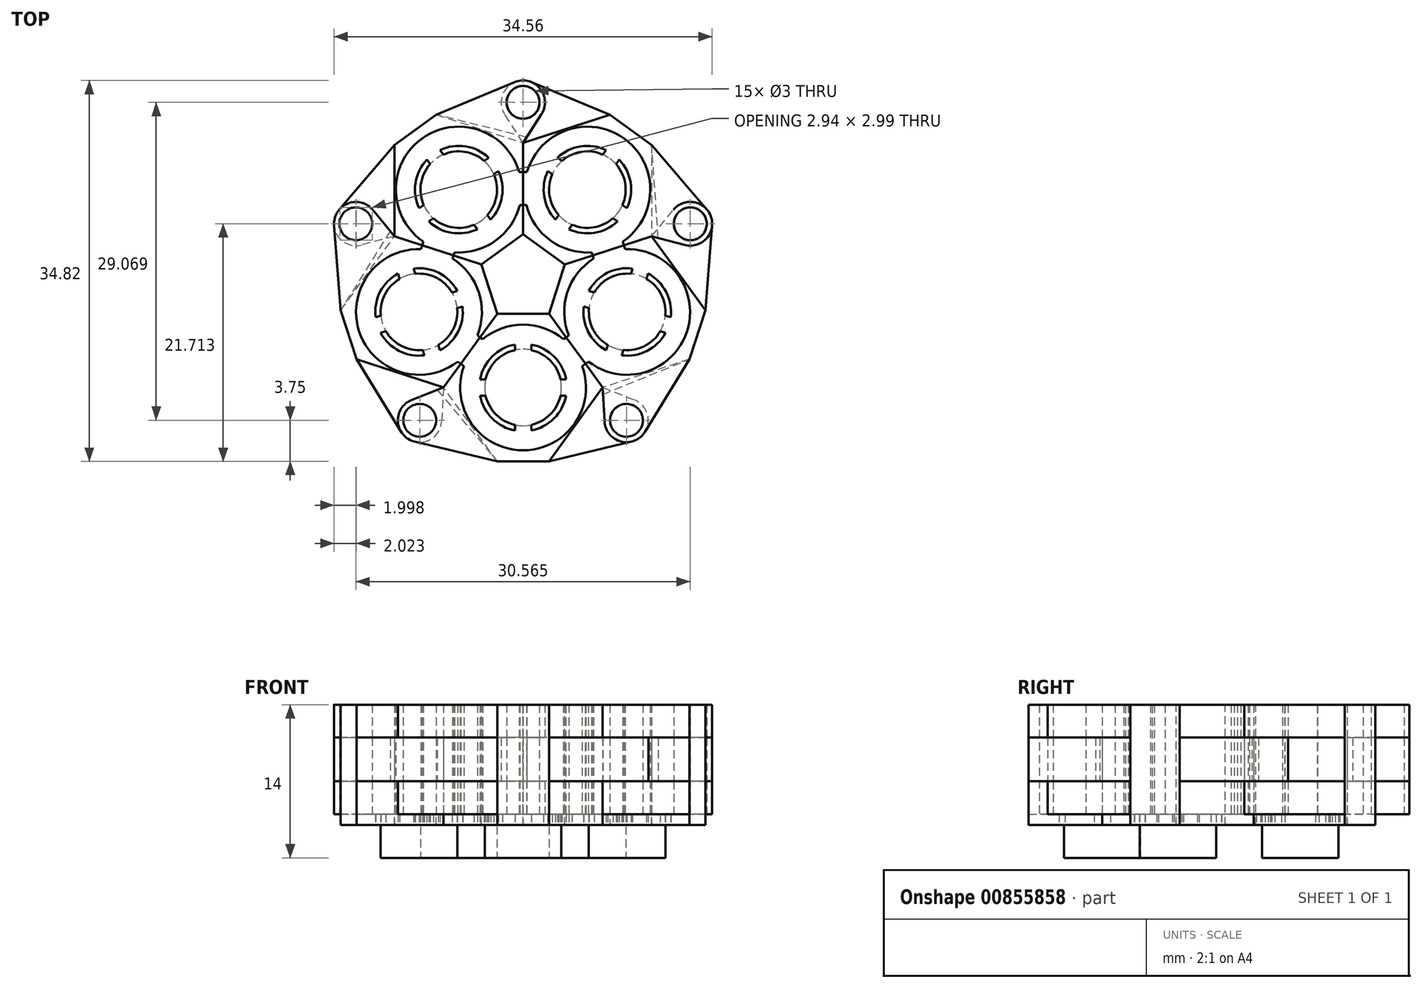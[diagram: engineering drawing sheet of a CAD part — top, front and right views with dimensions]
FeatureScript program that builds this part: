
annotation { "Feature Type Name" : "Feature", "Feature Type Description" : "" }
export const myFeature = defineFeature(function(context is Context, id is Id, definition is map)
    precondition{}
    {
        {
            var Q0;
            Q0=qCreatedBy(makeId("Top.planeOp"),FACE);
            var sketch = newSketch(context, id + "F0", { "sketchPlane" : qUnion([Q0])});
            skLineSegment(sketch, "E0.bottom", {"start": v(6.25, 6.75) * mm, "end": v(-6.25, 6.75) * mm});
            skLineSegment(sketch, "E0.top", {"start": v(6.25, -6.75) * mm, "end": v(-6.25, -6.75) * mm});
            skLineSegment(sketch, "E0.left", {"start": v(6.25, 6.75) * mm, "end": v(6.25, -6.75) * mm});
            skLineSegment(sketch, "E0.right", {"start": v(-6.25, 6.75) * mm, "end": v(-6.25, -6.75) * mm});
            skPoint(sketch, "E0.middle", {"position": v(0, 0) * mm});
            skCircle(sketch, "E1", {"center": v(0, 0) * mm, "radius": 5.75 * mm});
            skSolve(sketch);
        }
        {
            var Q0;
            Q0=qSketchRegion(id+"F0",true);
            extrude(context, id + "F1", {"entities" : qUnion([Q0]), "endBound" : BoundingType.SYMMETRIC, "depth" : 10 * mm, "offsetDistance" : 25 * mm});
        }
        {
            var Q0;
            Q0=qCreatedBy(makeId("Top.planeOp"),FACE);
            var sketch = newSketch(context, id + "F2", { "sketchPlane" : qUnion([Q0])});
            skLineSegment(sketch, "E2", {"start": v(-7.27, 0) * mm, "end": v(-4.76, -3.45) * mm});
            skLineSegment(sketch, "E3.MirrorCS", {"start": v(-7.27, 0) * mm, "end": v(-4.76, 3.45) * mm});
            skLineSegment(sketch, "E4.MirrorCS", {"start": v(7.27, 0) * mm, "end": v(4.76, -3.45) * mm});
            skLineSegment(sketch, "E5.MirrorCS", {"start": v(7.27, 0) * mm, "end": v(4.76, 3.45) * mm});
            skArc(sketch, "E6", {"start": v(-4.76, 3.45) * mm, "mid": v(-5.88, 0) * mm, "end": v(-4.76, -3.45) * mm});
            skPoint(sketch, "E7.orphan", {"position": v(-3, 5.88) * mm});
            skPoint(sketch, "E8.orphan", {"position": v(3, -5.88) * mm});
            skArc(sketch, "E9.trimOffspring", {"start": v(4.76, -3.45) * mm, "mid": v(5.88, 0) * mm, "end": v(4.76, 3.45) * mm});
            skPoint(sketch, "E10.orphan", {"position": v(-3, -5.88) * mm});
            skPoint(sketch, "E11.orphan", {"position": v(3, 5.88) * mm});
            skLineSegment(sketch, "E12", {"start": v(-4.76, 3.45) * mm, "end": v(0, 10) * mm, "construction": true});
            skLineSegment(sketch, "E13", {"start": v(0, 10) * mm, "end": v(4.76, 3.45) * mm, "construction": true});
            skSolve(sketch);
        }
        {
            var Q0;
            Q0=qSketchRegion(id+"F2",true);
            extrude(context, id + "F3", {"entities" : qUnion([Q0]), "operationType" : NewBodyOperationType.ADD, "endBound" : BoundingType.SYMMETRIC, "depth" : 10 * mm, "offsetDistance" : 25 * mm});
        }
        {
            var Q0;
            Q0=makeQuery(id+"F3.boolean.opBoolean","MERGE",FACE,{"derivedFrom":[makeQuery(id+"F1.opExtrude","CAP_FACE",FACE,{"disambiguationData":[OSD([sQuery(id+"F0.wireOp",EDGE,"E0.bottom"),sQuery(id+"F0.wireOp",EDGE,"E0.top"),sQuery(id+"F0.wireOp",EDGE,"E0.left"),sQuery(id+"F0.wireOp",EDGE,"E0.right"),sQuery(id+"F0.wireOp",EDGE,"E1")])],"isStart":false}),makeQuery(id+"F3.opExtrude","CAP_FACE",FACE,{"disambiguationData":[OSD([sQuery(id+"F2.wireOp",EDGE,"E2"),sQuery(id+"F2.wireOp",EDGE,"E3.MirrorCS"),sQuery(id+"F2.wireOp",EDGE,"E6")])],"isStart":false}),makeQuery(id+"F3.opExtrude","CAP_FACE",FACE,{"disambiguationData":[OSD([sQuery(id+"F2.wireOp",EDGE,"E4.MirrorCS"),sQuery(id+"F2.wireOp",EDGE,"E5.MirrorCS"),sQuery(id+"F2.wireOp",EDGE,"E9.trimOffspring")])],"isStart":false})]});
            var sketch = newSketch(context, id + "F4", { "sketchPlane" : qUnion([Q0])});
            skLineSegment(sketch, "E14.0", {"start": v(-7.27, 0) * mm, "end": v(-6.25, 1.4) * mm});
            skLineSegment(sketch, "E15", {"start": v(-6.25, 1.4) * mm, "end": v(-1.5, 7.94) * mm});
            skLineSegment(sketch, "E16.MirrorCS", {"start": v(-6.25, -1.4) * mm, "end": v(-1.5, -7.94) * mm});
            skLineSegment(sketch, "E17.MirrorCS", {"start": v(6.25, -1.4) * mm, "end": v(1.5, -7.94) * mm});
            skLineSegment(sketch, "E18.MirrorCS", {"start": v(6.25, 1.4) * mm, "end": v(1.5, 7.94) * mm});
            skLineSegment(sketch, "E19", {"start": v(-1.5, -7.94) * mm, "end": v(-8.25, -7.94) * mm});
            skLineSegment(sketch, "E20", {"start": v(-8.25, -7.94) * mm, "end": v(-6.25, -1.4) * mm});
            skLineSegment(sketch, "E21.MirrorCS", {"start": v(-8.25, 7.94) * mm, "end": v(-6.25, 1.4) * mm});
            skLineSegment(sketch, "E22.MirrorCS", {"start": v(-1.5, 7.94) * mm, "end": v(-8.25, 7.94) * mm});
            skLineSegment(sketch, "E23.MirrorCS", {"start": v(8.25, 7.94) * mm, "end": v(6.25, 1.4) * mm});
            skLineSegment(sketch, "E24.MirrorCS", {"start": v(1.5, 7.94) * mm, "end": v(8.25, 7.94) * mm});
            skLineSegment(sketch, "E25.MirrorCS", {"start": v(8.25, -7.94) * mm, "end": v(6.25, -1.4) * mm});
            skLineSegment(sketch, "E26.MirrorCS", {"start": v(1.5, -7.94) * mm, "end": v(8.25, -7.94) * mm});
            skSolve(sketch);
        }
        {
            var Q0;
            Q0 = qSketchRegion(id + "F4", true);
            extrude(context, id + "F5", {"entities" : qUnion([Q0]), "operationType" : NewBodyOperationType.REMOVE, "oppositeDirection" : true, "depth" : 25 * mm, "offsetDistance" : 25 * mm});
        }
        {
            var Q0;
            Q0=qCreatedBy(makeId("Top.planeOp"),FACE);
            var Q1;
            Q1=qCreatedBy(makeId("Top.planeOp"),FACE);
            var sketch = newSketch(context, id + "F6", { "sketchPlane" : qUnion([Q0, Q1])});
            skArc(sketch, "E27", {"start": v(-10.17, -1.14) * mm, "mid": v(-11.44, -3.14) * mm, "end": v(-9.91, -4.95) * mm});
            skLineSegment(sketch, "E28", {"start": v(-7.27, 0) * mm, "end": v(-10.17, -1.14) * mm});
            skLineSegment(sketch, "E29", {"start": v(-2.36, -6.75) * mm, "end": v(-9.91, -4.95) * mm});
            skCircle(sketch, "E30", {"center": v(-9.45, -3) * mm, "radius": 1.5 * mm});
            skLineSegment(sketch, "E31.0", {"start": v(-7.27, 0) * mm, "end": v(-2.36, 6.75) * mm, "construction": true});
            skLineSegment(sketch, "E32", {"start": v(-7.27, 0) * mm, "end": v(-12.6, -7.35) * mm, "construction": true});
            skLineSegment(sketch, "E33.trimOffspring", {"start": v(-2.57, -6.7) * mm, "end": v(-2.36, -6.75) * mm});
            skLineSegment(sketch, "E34.0", {"start": v(-7.27, 0) * mm, "end": v(-2.36, -6.75) * mm});
            skSolve(sketch);
        }
        {
            var Q0;
            Q0=makeQuery(id+"F6.imprint","IMPRINT",FACE,{"disambiguationData":[TD([[makeQuery(id+"F6.imprint","IMPRINT",EDGE,{"derivedFrom":sQuery(id+"F6.wireOp",EDGE,"346013c5-1229-483d-89d6-e8461794764b.0")}),1.0]])]});
            var Q1;
            Q1=makeQuery(id+"F6.imprint","IMPRINT",FACE,{"disambiguationData":[TD([[makeQuery(id+"F6.imprint","IMPRINT",EDGE,{"derivedFrom":sQuery(id+"F6.wireOp",EDGE,"E27")}),1.0]])]});
            extrude(context, id + "F7", {"entities" : qUnion([Q0, Q1]), "operationType" : NewBodyOperationType.ADD, "endBound" : BoundingType.SYMMETRIC, "depth" : 10 * mm, "offsetDistance" : 25 * mm});
        }
        {
            var Q0;
            Q0=makeQuery(id+"F7.boolean.opBoolean","MERGE",FACE,{"derivedFrom":[makeQuery(id+"F3.boolean.opBoolean","MERGE",FACE,{"derivedFrom":[makeQuery(id+"F1.opExtrude","CAP_FACE",FACE,{"disambiguationData":[OSD([sQuery(id+"F0.wireOp",EDGE,"E0.bottom"),sQuery(id+"F0.wireOp",EDGE,"E0.top"),sQuery(id+"F0.wireOp",EDGE,"E0.left"),sQuery(id+"F0.wireOp",EDGE,"E0.right"),sQuery(id+"F0.wireOp",EDGE,"E1")])],"isStart":true}),makeQuery(id+"F3.opExtrude","CAP_FACE",FACE,{"disambiguationData":[OSD([sQuery(id+"F2.wireOp",EDGE,"E2"),sQuery(id+"F2.wireOp",EDGE,"E3.MirrorCS"),sQuery(id+"F2.wireOp",EDGE,"E6")])],"isStart":true}),makeQuery(id+"F3.opExtrude","CAP_FACE",FACE,{"disambiguationData":[OSD([sQuery(id+"F2.wireOp",EDGE,"E4.MirrorCS"),sQuery(id+"F2.wireOp",EDGE,"E5.MirrorCS"),sQuery(id+"F2.wireOp",EDGE,"E9.trimOffspring")])],"isStart":true})]}),makeQuery(id+"F7.opExtrude","CAP_FACE",FACE,{"disambiguationData":[OSD([sQuery(id+"F6.wireOp",EDGE,"E27"),sQuery(id+"F6.wireOp",EDGE,"E28"),sQuery(id+"F6.wireOp",EDGE,"E29"),sQuery(id+"F6.wireOp",EDGE,"E30"),sQuery(id+"F6.wireOp",EDGE,"E33.trimOffspring"),sQuery(id+"F6.wireOp",EDGE,"E34.0")])],"isStart":true})]});
            var sketch = newSketch(context, id + "F8", { "sketchPlane" : qUnion([Q0])});
            skLineSegment(sketch, "E35.0", {"start": v(7.27, 0) * mm, "end": v(2.36, 6.75) * mm});
            skLineSegment(sketch, "E36.0", {"start": v(7.27, 0) * mm, "end": v(2.36, -6.75) * mm});
            skLineSegment(sketch, "E37.0", {"start": v(2.36, -6.75) * mm, "end": v(-2.36, -6.75) * mm});
            skLineSegment(sketch, "E38.0", {"start": v(-7.27, 0) * mm, "end": v(-2.36, -6.75) * mm});
            skLineSegment(sketch, "E39.0", {"start": v(2.36, 6.75) * mm, "end": v(-2.36, 6.75) * mm});
            skLineSegment(sketch, "E40", {"start": v(-2.36, 6.75) * mm, "end": v(-7.27, 0) * mm});
            skSolve(sketch);
        }
        {
            var Q0;
            Q0 = qSketchRegion(id + "F8", true);
            extrude(context, id + "F9", {"entities" : qUnion([Q0]), "operationType" : NewBodyOperationType.ADD, "depth" : 1 * mm, "offsetDistance" : 25 * mm});
        }
        {
            var Q0;
            Q0=qCreatedBy(makeId("Top.planeOp"),FACE);
            var Q1;
            Q1=qCreatedBy(makeId("Top.planeOp"),FACE);
            var sketch = newSketch(context, id + "F10", { "sketchPlane" : qUnion([Q0, Q1])});
            skLineSegment(sketch, "E41.0", {"start": v(2.36, -6.75) * mm, "end": v(7.27, 0) * mm});
            skArc(sketch, "E42", {"start": v(9.91, -4.95) * mm, "mid": v(11.44, -3.14) * mm, "end": v(10.17, -1.14) * mm});
            skLineSegment(sketch, "E43", {"start": v(7.27, 0) * mm, "end": v(10.17, -1.14) * mm});
            skLineSegment(sketch, "E44", {"start": v(2.36, -6.75) * mm, "end": v(9.91, -4.95) * mm});
            skCircle(sketch, "E45", {"center": v(9.45, -3) * mm, "radius": 1.5 * mm});
            skLineSegment(sketch, "E46.0", {"start": v(7.27, 0) * mm, "end": v(3.56, 5.1) * mm, "construction": true});
            skLineSegment(sketch, "E47", {"start": v(7.27, 0) * mm, "end": v(12.82, -7.64) * mm, "construction": true});
            skSolve(sketch);
        }
        {
            var Q0;
            Q0=qSketchRegion(id+"F10",true);
            extrude(context, id + "F11", {"entities" : qUnion([Q0]), "operationType" : NewBodyOperationType.ADD, "endBound" : BoundingType.SYMMETRIC, "depth" : 4 * mm, "offsetDistance" : 25 * mm});
        }
        {
            var Q0;
            Q0=makeQuery(id+"F7.boolean.opBoolean","MERGE",EDGE,{"derivedFrom":[makeQuery(id+"F3.boolean.opBoolean","MERGE",EDGE,{"derivedFrom":[makeQuery(id+"F1.opExtrude","SWEPT_EDGE",EDGE,{"disambiguationData":[OSD([sQuery(id+"F0.wireOp",EDGE,"E0.top"),sQuery(id+"F0.wireOp",EDGE,"E0.right")])]}),makeQuery(id+"F3.opExtrude","SWEPT_EDGE",EDGE,{"disambiguationData":[OSD([sQuery(id+"F2.wireOp",EDGE,"c5022347-942f-4ce8-8673-535321e667700.MirrorCS"),sQuery(id+"F2.wireOp",EDGE,"c5022347-942f-4ce8-8673-535321e667702.MirrorCS")])]})]}),makeQuery(id+"F7.opExtrude","SWEPT_EDGE",EDGE,{"disambiguationData":[OSD([sQuery(id+"F6.wireOp",EDGE,"346013c5-1229-483d-89d6-e8461794764b.0"),sQuery(id+"F6.wireOp",EDGE,"E29")])]})]});
            var Q1;
            Q1=makeQuery(id+"F7.boolean.opBoolean","MERGE",EDGE,{"derivedFrom":[makeQuery(id+"F5.boolean.opBoolean","INTERSECT",EDGE,{"derivedFrom":[makeQuery(id+"F1.opExtrude","SWEPT_FACE",FACE,{"disambiguationData":[OSD([sQuery(id+"F0.wireOp",EDGE,"E0.top")])]}),makeQuery(id+"F5.opExtrude","SWEPT_FACE",FACE,{"disambiguationData":[OSD([sQuery(id+"F4.wireOp",EDGE,"E16.MirrorCS")])]})]}),makeQuery(id+"F7.opExtrude","SWEPT_EDGE",EDGE,{"disambiguationData":[OSD([sQuery(id+"F6.wireOp",EDGE,"E33.trimOffspring"),sQuery(id+"F6.wireOp",EDGE,"E34.0")])]})]});
            cPlane(context, id + "F12", {"entities" : qUnion([Q0, Q1]), "cplaneType" : CPlaneType.LINE_ANGLE, "offset" : 25 * mm, "angle" : 50 * degree, "width" : 150 * mm, "height" : 150 * mm});
        }
        {
            var Q0;
            Q0=qCreatedBy(id+"F12.planeOp",FACE);
            var sketch = newSketch(context, id + "F13", { "sketchPlane" : qUnion([Q0])});
            skLineSegment(sketch, "E48.0", {"start": v(6.15, 2) * mm, "end": v(6.15, -2) * mm});
            skLineSegment(sketch, "E49", {"start": v(6.15, 2) * mm, "end": v(12.33, 2) * mm});
            skLineSegment(sketch, "E50.MirrorCS", {"start": v(6.15, -2) * mm, "end": v(12.33, -2) * mm});
            skLineSegment(sketch, "E51", {"start": v(12.33, -2) * mm, "end": v(12.33, 2) * mm});
            skPoint(sketch, "E52.orphan", {"position": v(6.15, 5) * mm});
            skPoint(sketch, "E53.orphan", {"position": v(6.15, -5) * mm});
            skSolve(sketch);
        }
        {
            var Q0;
            Q0=qSketchRegion(id+"F13",true);
            extrude(context, id + "F14", {"entities" : qUnion([Q0]), "operationType" : NewBodyOperationType.REMOVE, "depth" : 25 * mm, "offsetDistance" : 25 * mm});
        }
        {
            var Q0;
            Q0=qCreatedBy(makeId("Right.planeOp"),FACE);
            var sketch = newSketch(context, id + "F15", { "sketchPlane" : qUnion([Q0])});
            skLineSegment(sketch, "E54", {"start": v(10, 4.4) * mm, "end": v(10, -5.35) * mm});
            skSolve(sketch);
        }
        {
            var Q0;
            Q0=makeQuery(id+"F7.boolean.opBoolean","MERGE",FACE,{"derivedFrom":[makeQuery(id+"F3.boolean.opBoolean","MERGE",FACE,{"derivedFrom":[makeQuery(id+"F1.opExtrude","CAP_FACE",FACE,{"disambiguationData":[OSD([sQuery(id+"F0.wireOp",EDGE,"E0.bottom"),sQuery(id+"F0.wireOp",EDGE,"E0.top"),sQuery(id+"F0.wireOp",EDGE,"E0.left"),sQuery(id+"F0.wireOp",EDGE,"E0.right"),sQuery(id+"F0.wireOp",EDGE,"E1")])],"isStart":false}),makeQuery(id+"F3.opExtrude","CAP_FACE",FACE,{"disambiguationData":[OSD([sQuery(id+"F2.wireOp",EDGE,"E2"),sQuery(id+"F2.wireOp",EDGE,"E3.MirrorCS"),sQuery(id+"F2.wireOp",EDGE,"E6")])],"isStart":false}),makeQuery(id+"F3.opExtrude","CAP_FACE",FACE,{"disambiguationData":[OSD([sQuery(id+"F2.wireOp",EDGE,"E4.MirrorCS"),sQuery(id+"F2.wireOp",EDGE,"E5.MirrorCS"),sQuery(id+"F2.wireOp",EDGE,"E9.trimOffspring")])],"isStart":false})]}),makeQuery(id+"F7.opExtrude","CAP_FACE",FACE,{"disambiguationData":[OSD([sQuery(id+"F6.wireOp",EDGE,"E27"),sQuery(id+"F6.wireOp",EDGE,"E28"),sQuery(id+"F6.wireOp",EDGE,"E29"),sQuery(id+"F6.wireOp",EDGE,"E30"),sQuery(id+"F6.wireOp",EDGE,"E33.trimOffspring"),sQuery(id+"F6.wireOp",EDGE,"E34.0")])],"isStart":false})]});
            var sketch = newSketch(context, id + "F16", { "sketchPlane" : qUnion([Q0])});
            skLineSegment(sketch, "E55", {"start": v(0, 0) * mm, "end": v(-9.47, 6.63) * mm, "construction": true});
            skLineSegment(sketch, "E56", {"start": v(-8.24, 3.94) * mm, "end": v(-3.26, 0.45) * mm});
            skLineSegment(sketch, "E57.MirrorCS", {"start": v(-6.52, 6.4) * mm, "end": v(-1.54, 2.9) * mm});
            skLineSegment(sketch, "E58.MirrorCS", {"start": v(6.52, 6.4) * mm, "end": v(1.54, 2.9) * mm});
            skLineSegment(sketch, "E59.MirrorCS", {"start": v(8.24, 3.94) * mm, "end": v(3.26, 0.45) * mm});
            skLineSegment(sketch, "E60", {"start": v(-8.24, 3.94) * mm, "end": v(-6.52, 6.4) * mm});
            skLineSegment(sketch, "E61", {"start": v(-3.26, 0.45) * mm, "end": v(-1.54, 2.9) * mm});
            skLineSegment(sketch, "E62", {"start": v(1.54, 2.9) * mm, "end": v(3.26, 0.45) * mm});
            skLineSegment(sketch, "E63", {"start": v(6.52, 6.4) * mm, "end": v(8.24, 3.94) * mm});
            skSolve(sketch);
        }
        {
            var Q0;
            Q0 = qSketchRegion(id + "F16", true);
            extrude(context, id + "F17", {"entities" : qUnion([Q0]), "operationType" : NewBodyOperationType.REMOVE, "oppositeDirection" : true, "depth" : 10 * mm, "offsetDistance" : 25 * mm});
        }
        {
            var Q0;
            Q0=makeQuery(id+"F9.boolean.opBoolean","MERGE",FACE,{"derivedFrom":[makeQuery(id+"F1.opExtrude","SWEPT_FACE",FACE,{"disambiguationData":[OSD([sQuery(id+"F0.wireOp",EDGE,"E0.top")])]}),makeQuery(id+"F9.opExtrude","SWEPT_FACE",FACE,{"disambiguationData":[OSD([sQuery(id+"F8.wireOp",EDGE,"E39.0")])]})]});
            var sketch = newSketch(context, id + "F18", { "sketchPlane" : qUnion([Q0])});
            skLineSegment(sketch, "E64", {"start": v(-2.36, 2) * mm, "end": v(-2.36, -5) * mm});
            skLineSegment(sketch, "E65", {"start": v(-2.36, -5) * mm, "end": v(2.36, -5) * mm});
            skLineSegment(sketch, "E66", {"start": v(2.36, -5) * mm, "end": v(2.36, 2) * mm});
            skLineSegment(sketch, "E67", {"start": v(2.36, 2) * mm, "end": v(-2.36, 2) * mm});
            skSolve(sketch);
        }
        {
            var Q0;
            Q0=makeQuery(id+"F9.opExtrude","CAP_FACE",FACE,{"disambiguationData":[OSD([sQuery(id+"F8.wireOp",EDGE,"E35.0"),sQuery(id+"F8.wireOp",EDGE,"E36.0"),sQuery(id+"F8.wireOp",EDGE,"E37.0"),sQuery(id+"F8.wireOp",EDGE,"E38.0"),sQuery(id+"F8.wireOp",EDGE,"E39.0"),sQuery(id+"F8.wireOp",EDGE,"E40")])],"isStart":false});
            var sketch = newSketch(context, id + "F19", { "sketchPlane" : qUnion([Q0])});
            skArc(sketch, "E68", {"start": v(-0.75, 3.42) * mm, "mid": v(-2.47, 2.47) * mm, "end": v(-3.42, 0.75) * mm});
            skLineSegment(sketch, "E69", {"start": v(-0.75, 3.42) * mm, "end": v(-0.75, 3.93) * mm});
            skLineSegment(sketch, "E70.MirrorCS", {"start": v(0.75, 3.42) * mm, "end": v(0.75, 3.93) * mm});
            skLineSegment(sketch, "E71.MirrorCS", {"start": v(-0.75, -3.42) * mm, "end": v(-0.75, -3.93) * mm});
            skLineSegment(sketch, "E72.MirrorCS", {"start": v(0.75, -3.42) * mm, "end": v(0.75, -3.93) * mm});
            skLineSegment(sketch, "E73", {"start": v(3.42, -0.75) * mm, "end": v(3.93, -0.75) * mm});
            skLineSegment(sketch, "E74.MirrorCS", {"start": v(3.42, 0.75) * mm, "end": v(3.93, 0.75) * mm});
            skLineSegment(sketch, "E75.MirrorCS", {"start": v(-3.42, 0.75) * mm, "end": v(-3.93, 0.75) * mm});
            skLineSegment(sketch, "E76.MirrorCS", {"start": v(-3.42, -0.75) * mm, "end": v(-3.93, -0.75) * mm});
            skArc(sketch, "E77", {"start": v(-0.75, 3.93) * mm, "mid": v(-2.83, 2.83) * mm, "end": v(-3.93, 0.75) * mm});
            skArc(sketch, "E78.trimOffspring", {"start": v(-0.75, 3.93) * mm, "mid": v(-2.66, 2.66) * mm, "end": v(-3.93, 0.75) * mm, "construction": true});
            skArc(sketch, "E79.trimOffspring", {"start": v(-3.42, -0.75) * mm, "mid": v(-2.47, -2.47) * mm, "end": v(-0.75, -3.42) * mm});
            skArc(sketch, "E80.trimOffspring", {"start": v(-3.93, -0.75) * mm, "mid": v(-2.83, -2.83) * mm, "end": v(-0.75, -3.93) * mm});
            skArc(sketch, "E81.trimOffspring", {"start": v(0.75, -3.42) * mm, "mid": v(2.47, -2.47) * mm, "end": v(3.42, -0.75) * mm});
            skArc(sketch, "E82.trimOffspring", {"start": v(3.42, 0.75) * mm, "mid": v(2.47, 2.47) * mm, "end": v(0.75, 3.42) * mm});
            skArc(sketch, "E83.trimOffspring", {"start": v(3.93, 0.75) * mm, "mid": v(2.83, 2.83) * mm, "end": v(0.75, 3.93) * mm});
            skPoint(sketch, "E84.0.start.orphan", {"position": v(3.69, -4.41) * mm});
            skPoint(sketch, "E85.trimOffspring.end.orphan", {"position": v(-3.69, -4.41) * mm});
            skArc(sketch, "E86.trimOffspring", {"start": v(0.75, -3.93) * mm, "mid": v(2.83, -2.83) * mm, "end": v(3.93, -0.75) * mm});
            skSolve(sketch);
        }
        {
            var Q0;
            Q0 = qSketchRegion(id + "F19", true);
            extrude(context, id + "F20", {"entities" : qUnion([Q0]), "operationType" : NewBodyOperationType.REMOVE, "oppositeDirection" : true, "depth" : 25 * mm, "offsetDistance" : 25 * mm});
        }
        {
            var Q0;
            Q0=makeQuery(id+"F9.opExtrude","CAP_FACE",FACE,{"disambiguationData":[OSD([sQuery(id+"F8.wireOp",EDGE,"E35.0"),sQuery(id+"F8.wireOp",EDGE,"E36.0"),sQuery(id+"F8.wireOp",EDGE,"E37.0"),sQuery(id+"F8.wireOp",EDGE,"E38.0"),sQuery(id+"F8.wireOp",EDGE,"E39.0"),sQuery(id+"F8.wireOp",EDGE,"E40")])],"isStart":false});
            var sketch = newSketch(context, id + "F21", { "sketchPlane" : qUnion([Q0])});
            skCircle(sketch, "E87", {"center": v(0, 0) * mm, "radius": 3.5 * mm});
            skSolve(sketch);
        }
        {
            var Q0;
            Q0 = qSketchRegion(id + "F21", true);
            extrude(context, id + "F22", {"entities" : qUnion([Q0]), "operationType" : NewBodyOperationType.ADD, "depth" : 3 * mm, "offsetDistance" : 25 * mm});
        }
        {
            var Q0;
            Q0=makeQuery(id+"F1.opExtrude","SWEPT_BODY",BODY,{"disambiguationData":[OSD([sQuery(id+"F0.wireOp",EDGE,"E0.bottom"),sQuery(id+"F0.wireOp",EDGE,"E0.top"),sQuery(id+"F0.wireOp",EDGE,"E0.left"),sQuery(id+"F0.wireOp",EDGE,"E0.right"),sQuery(id+"F0.wireOp",EDGE,"E1")])]});
            var Q1;
            Q1=sQuery(id+"F15.wireOp",EDGE,"E54");
            circularPattern(context, id + "F23", {"entities" : qUnion([Q0]), "axis" : qUnion([Q1]), "angle" : 360 * degree, "instanceCount" : 5, "equalSpace" : true});
        }
    });
